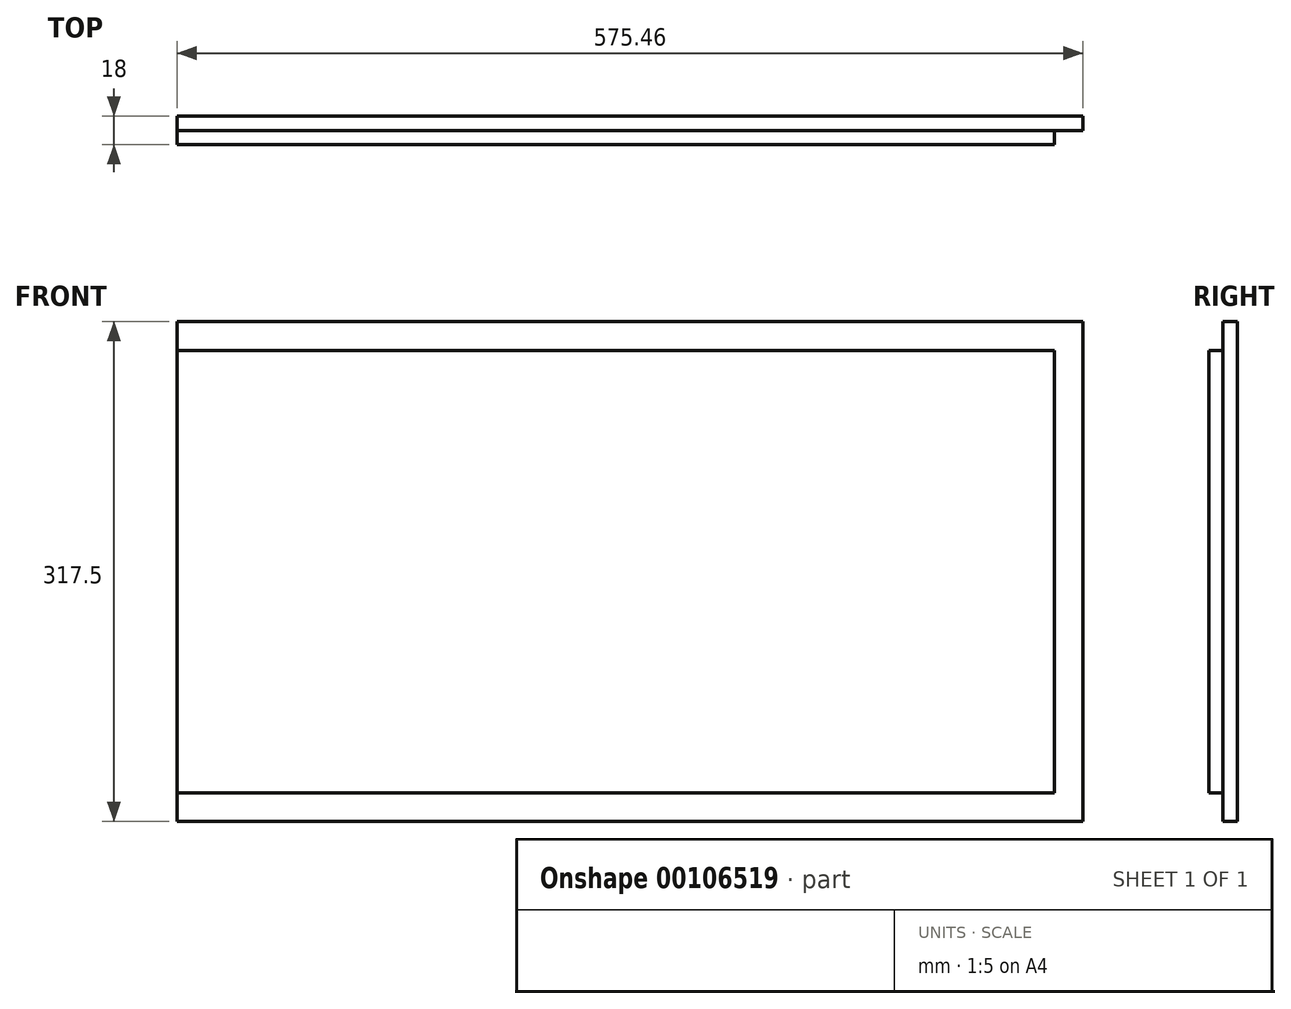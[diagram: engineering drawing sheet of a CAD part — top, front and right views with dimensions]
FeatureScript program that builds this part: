
annotation { "Feature Type Name" : "Feature", "Feature Type Description" : "" }
export const myFeature = defineFeature(function(context is Context, id is Id, definition is map)
    precondition{}
    {
        {
            var Q0;
            Q0=qCreatedBy(makeId("Front.planeOp"),FACE);
            var sketch = newSketch(context, id + "F0", { "sketchPlane" : qUnion([Q0])});
            skLineSegment(sketch, "E0.bottom", {"start": v(287.73, -158.75) * mm, "end": v(-287.73, -158.75) * mm});
            skLineSegment(sketch, "E0.top", {"start": v(287.73, 158.75) * mm, "end": v(-287.73, 158.75) * mm});
            skLineSegment(sketch, "E0.left", {"start": v(287.73, -158.75) * mm, "end": v(287.73, 158.75) * mm});
            skLineSegment(sketch, "E0.right", {"start": v(-287.73, -158.75) * mm, "end": v(-287.73, 158.75) * mm});
            skPoint(sketch, "E0.middle", {"position": v(0, 0) * mm});
            skSolve(sketch);
        }
        {
            var Q0;
            Q0=makeQuery(id+"F0.imprint","IMPRINT",FACE,{"disambiguationData":[TD([[makeQuery(id+"F0.imprint","IMPRINT",EDGE,{"derivedFrom":sQuery(id+"F0.wireOp",EDGE,"E0.bottom")}),-1.0]])]});
            extrude(context, id + "F1", {"entities" : qUnion([Q0]), "depth" : 18 * mm});
        }
        {
            var Q0;
            Q0=makeQuery(id+"F1.opExtrude","CAP_FACE",FACE,{"disambiguationData":[OSD([sQuery(id+"F0.wireOp",EDGE,"E0.bottom"),sQuery(id+"F0.wireOp",EDGE,"E0.top"),sQuery(id+"F0.wireOp",EDGE,"E0.left"),sQuery(id+"F0.wireOp",EDGE,"E0.right")])],"isStart":false});
            var sketch = newSketch(context, id + "F2", { "sketchPlane" : qUnion([Q0])});
            skLineSegment(sketch, "E1.0", {"start": v(287.73, 158.75) * mm, "end": v(-287.73, 158.75) * mm});
            skLineSegment(sketch, "E2.0", {"start": v(287.73, -158.75) * mm, "end": v(287.73, 158.75) * mm});
            skLineSegment(sketch, "E3.0", {"start": v(287.73, -158.75) * mm, "end": v(-287.73, -158.75) * mm});
            skLineSegment(sketch, "E4.0", {"start": v(-287.73, -158.75) * mm, "end": v(-287.73, -140.5) * mm});
            skLineSegment(sketch, "E5.0", {"start": v(269.48, 140.5) * mm, "end": v(-287.73, 140.5) * mm});
            skLineSegment(sketch, "E6.0", {"start": v(269.48, -140.5) * mm, "end": v(269.48, 140.5) * mm});
            skLineSegment(sketch, "E7.0", {"start": v(269.48, -140.5) * mm, "end": v(-287.73, -140.5) * mm});
            skLineSegment(sketch, "E8.trimOffspring", {"start": v(-287.73, 140.5) * mm, "end": v(-287.73, 158.75) * mm});
            skSolve(sketch);
        }
        {
            var Q0;
            Q0=makeQuery(id+"F2.imprint","IMPRINT",FACE,{"disambiguationData":[TD([[makeQuery(id+"F2.imprint","IMPRINT",EDGE,{"derivedFrom":sQuery(id+"F2.wireOp",EDGE,"E1.0")}),1.0]])]});
            extrude(context, id + "F3", {"entities" : qUnion([Q0]), "operationType" : NewBodyOperationType.REMOVE, "oppositeDirection" : true, "depth" : 8.73 * mm});
        }
    });
